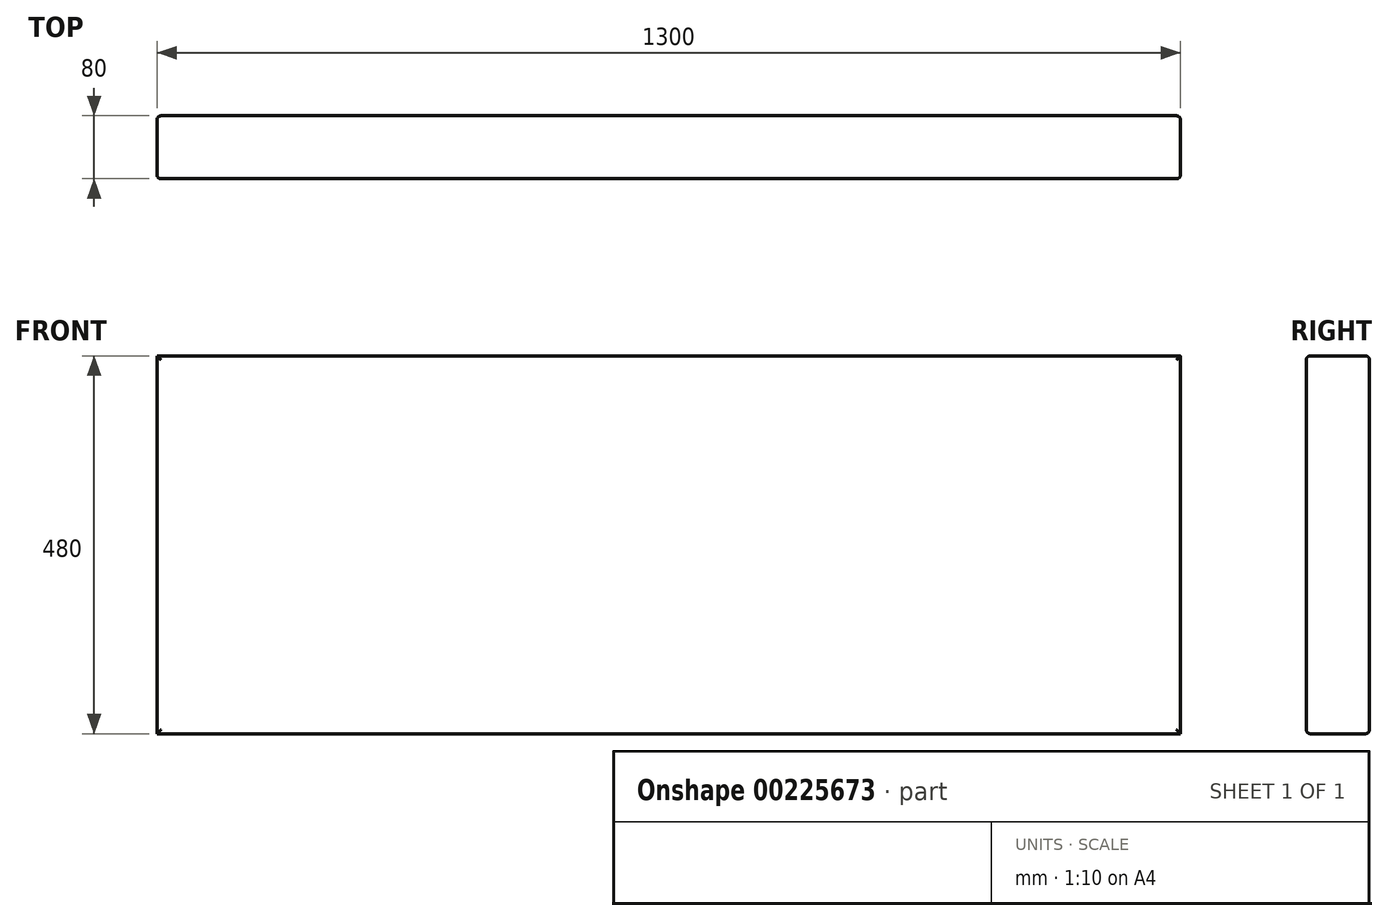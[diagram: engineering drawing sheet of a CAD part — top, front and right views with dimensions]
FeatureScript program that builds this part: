
annotation { "Feature Type Name" : "Feature", "Feature Type Description" : "" }
export const myFeature = defineFeature(function(context is Context, id is Id, definition is map)
    precondition{}
    {
        {
            var Q0;
            Q0=qCreatedBy(makeId("Front.planeOp"),FACE);
            var sketch = newSketch(context, id + "F0", { "sketchPlane" : qUnion([Q0])});
            skLineSegment(sketch, "E0.bottom", {"start": v(-650, 240) * mm, "end": v(650, 240) * mm});
            skLineSegment(sketch, "E0.top", {"start": v(-650, -240) * mm, "end": v(650, -240) * mm});
            skLineSegment(sketch, "E0.left", {"start": v(-650, 240) * mm, "end": v(-650, -240) * mm});
            skLineSegment(sketch, "E0.right", {"start": v(650, 240) * mm, "end": v(650, -240) * mm});
            skLineSegment(sketch, "E1", {"start": v(0, 240) * mm, "end": v(0, -240) * mm, "construction": true});
            skLineSegment(sketch, "E2", {"start": v(-650, 0) * mm, "end": v(650, 0) * mm, "construction": true});
            skSolve(sketch);
        }
        {
            var Q0;
            Q0=makeQuery(id+"F0.imprint","IMPRINT",FACE,{"disambiguationData":[TD([[makeQuery(id+"F0.imprint","IMPRINT",EDGE,{"derivedFrom":sQuery(id+"F0.wireOp",EDGE,"E0.bottom")}),-1.0]])]});
            extrude(context, id + "F1", {"entities" : qUnion([Q0]), "endBound" : BoundingType.SYMMETRIC, "depth" : 80 * mm});
        }
        {
            var Q0;
            Q0=makeQuery(id+"F1.opExtrude","CAP_EDGE",EDGE,{"disambiguationData":[OSD([sQuery(id+"F0.wireOp",EDGE,"E0.bottom")])],"isStart":false});
            var Q1;
            Q1=makeQuery(id+"F1.opExtrude","CAP_EDGE",EDGE,{"disambiguationData":[OSD([sQuery(id+"F0.wireOp",EDGE,"E0.right")])],"isStart":false});
            var Q2;
            Q2=makeQuery(id+"F1.opExtrude","CAP_EDGE",EDGE,{"disambiguationData":[OSD([sQuery(id+"F0.wireOp",EDGE,"E0.top")])],"isStart":false});
            var Q3;
            Q3=makeQuery(id+"F1.opExtrude","CAP_EDGE",EDGE,{"disambiguationData":[OSD([sQuery(id+"F0.wireOp",EDGE,"E0.left")])],"isStart":false});
            var Q4;
            Q4=makeQuery(id+"F1.opExtrude","CAP_EDGE",EDGE,{"disambiguationData":[OSD([sQuery(id+"F0.wireOp",EDGE,"E0.bottom")])],"isStart":true});
            var Q5;
            Q5=makeQuery(id+"F1.opExtrude","CAP_EDGE",EDGE,{"disambiguationData":[OSD([sQuery(id+"F0.wireOp",EDGE,"E0.right")])],"isStart":true});
            var Q6;
            Q6=makeQuery(id+"F1.opExtrude","CAP_EDGE",EDGE,{"disambiguationData":[OSD([sQuery(id+"F0.wireOp",EDGE,"E0.top")])],"isStart":true});
            var Q7;
            Q7=makeQuery(id+"F1.opExtrude","CAP_EDGE",EDGE,{"disambiguationData":[OSD([sQuery(id+"F0.wireOp",EDGE,"E0.left")])],"isStart":true});
            fillet(context, id + "F2", {"entities" : qUnion([Q0, Q1, Q2, Q3, Q4, Q5, Q6, Q7]), "radius" : 5 * mm, "tangentPropagation" : true, "allowEdgeOverflow" : false});
        }
    });
